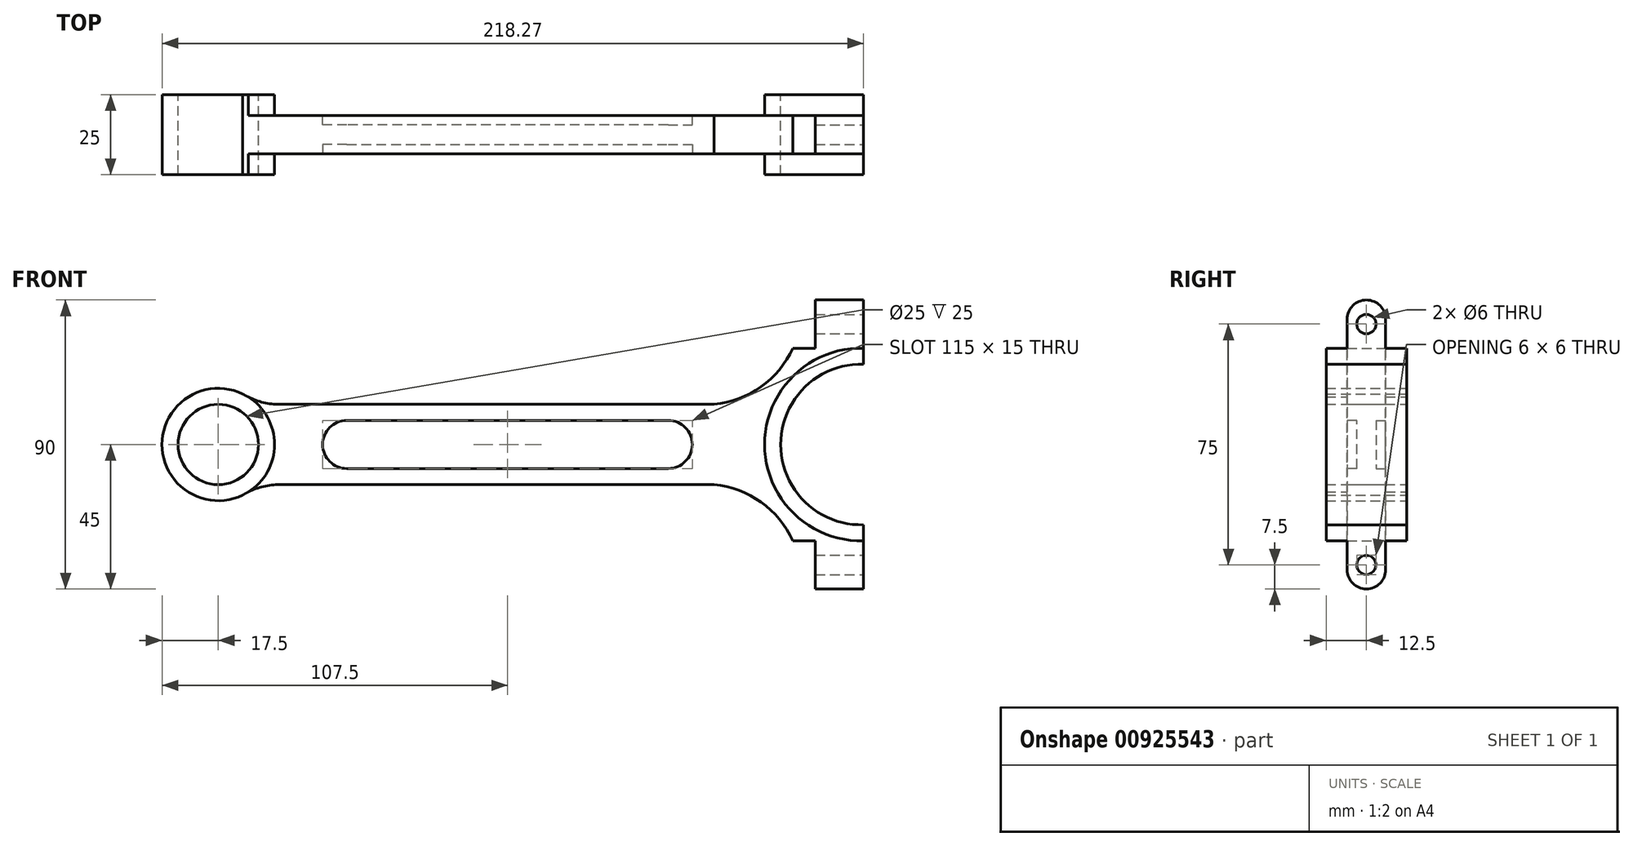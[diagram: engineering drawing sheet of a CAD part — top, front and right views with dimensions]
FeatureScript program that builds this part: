
annotation { "Feature Type Name" : "Feature", "Feature Type Description" : "" }
export const myFeature = defineFeature(function(context is Context, id is Id, definition is map)
    precondition{}
    {
        {
            var Q0;
            Q0=qCreatedBy(makeId("Front.planeOp"),FACE);
            var sketch = newSketch(context, id + "F0", { "sketchPlane" : qUnion([Q0])});
            skLineSegment(sketch, "E0", {"start": v(-127.43, 0) * mm, "end": v(160.56, 0) * mm, "construction": true});
            skCircle(sketch, "E1", {"center": v(-89.8, 0) * mm, "radius": 12.5 * mm});
            skCircle(sketch, "E2", {"center": v(-89.8, 0) * mm, "radius": 17.5 * mm});
            skArc(sketch, "E3", {"start": v(110.97, 24.99) * mm, "mid": v(85.2, 0) * mm, "end": v(110.97, -24.99) * mm});
            skLineSegment(sketch, "E4", {"start": v(110.97, -45) * mm, "end": v(95.97, -45) * mm});
            skLineSegment(sketch, "E5", {"start": v(95.97, -45) * mm, "end": v(95.97, -30) * mm});
            skLineSegment(sketch, "E6", {"start": v(110.97, 45) * mm, "end": v(95.97, 45) * mm});
            skLineSegment(sketch, "E7", {"start": v(95.97, 45) * mm, "end": v(95.97, 30) * mm});
            skLineSegment(sketch, "E8", {"start": v(95.97, 30) * mm, "end": v(88.97, 30) * mm});
            skLineSegment(sketch, "E9", {"start": v(95.97, -30) * mm, "end": v(88.97, -30) * mm});
            skLineSegment(sketch, "E10", {"start": v(110.97, 45) * mm, "end": v(110.97, 24.99) * mm});
            skLineSegment(sketch, "E11", {"start": v(110.97, -24.99) * mm, "end": v(110.97, -45) * mm});
            skArc(sketch, "E12", {"start": v(64.45, 12.5) * mm, "mid": v(79.06, 17.95) * mm, "end": v(88.97, 30) * mm});
            skArc(sketch, "E13", {"start": v(88.97, -30) * mm, "mid": v(79.06, -17.95) * mm, "end": v(64.45, -12.5) * mm});
            skLineSegment(sketch, "E14", {"start": v(64.45, 12.5) * mm, "end": v(-70.67, 12.5) * mm});
            skLineSegment(sketch, "E15", {"start": v(-70.67, -12.5) * mm, "end": v(64.45, -12.5) * mm});
            skArc(sketch, "E16", {"start": v(-82.18, 15.75) * mm, "mid": v(-76.65, 13.33) * mm, "end": v(-70.67, 12.5) * mm});
            skArc(sketch, "E17", {"start": v(-70.67, -12.5) * mm, "mid": v(-76.65, -13.33) * mm, "end": v(-82.18, -15.75) * mm});
            skArc(sketch, "E18", {"start": v(110.97, 30) * mm, "mid": v(80.2, 0) * mm, "end": v(110.97, -30) * mm});
            skSolve(sketch);
        }
        {
            var Q0;
            {var subQ0=sQuery(id+"F0.wireOp",EDGE,"E3");Q0=makeQuery(id+"F0.imprint","IMPRINT",FACE,{"disambiguationData":[TD([[makeQuery(id+"F0.imprint","IMPRINT",EDGE,{"derivedFrom":subQ0}),-1.0]])]});}
            var Q1;
            Q1=makeQuery(id+"F0.imprint","IMPRINT",FACE,{"disambiguationData":[TD([[makeQuery(id+"F0.imprint","IMPRINT",EDGE,{"derivedFrom":sQuery(id+"F0.wireOp",EDGE,"E1")}),-1.0]])]});
            extrude(context, id + "F1", {"entities" : qUnion([Q0, Q1]), "depth" : 25 * mm, "offsetDistance" : 25 * mm, "symmetric" : true});
        }
        {
            var Q0;
            {var subQ4=sQuery(id+"F0.wireOp",EDGE,"E4");Q0=makeQuery(id+"F0.imprint","IMPRINT",FACE,{"disambiguationData":[TD([[makeQuery(id+"F0.imprint","IMPRINT",EDGE,{"derivedFrom":subQ4}),-1.0]])]});}
            extrude(context, id + "F2", {"entities" : qUnion([Q0]), "operationType" : NewBodyOperationType.ADD, "depth" : 12 * mm, "offsetDistance" : 25 * mm, "symmetric" : true});
        }
        {
            var Q0;
            Q0=makeQuery(id+"F2.opExtrude","CAP_EDGE",EDGE,{"disambiguationData":[OSD([sQuery(id+"F0.wireOp",EDGE,"E6")])],"isStart":false});
            var Q1;
            Q1=makeQuery(id+"F2.opExtrude","CAP_EDGE",EDGE,{"disambiguationData":[OSD([sQuery(id+"F0.wireOp",EDGE,"E6")])],"isStart":true});
            fillet(context, id + "F3", {"entities" : qUnion([Q0, Q1]), "radius" : 6 * mm, "tangentPropagation" : true, "allowEdgeOverflow" : false});
        }
        {
            var Q0;
            Q0=makeQuery(id+"F2.opExtrude","CAP_EDGE",EDGE,{"disambiguationData":[OSD([sQuery(id+"F0.wireOp",EDGE,"E4")])],"isStart":false});
            var Q1;
            Q1=makeQuery(id+"F2.opExtrude","CAP_EDGE",EDGE,{"disambiguationData":[OSD([sQuery(id+"F0.wireOp",EDGE,"E4")])],"isStart":true});
            fillet(context, id + "F4", {"entities" : qUnion([Q0, Q1]), "radius" : 6 * mm, "tangentPropagation" : true, "allowEdgeOverflow" : false});
        }
        {
            var Q0;
            Q0=makeQuery(id+"F2.opExtrude","CAP_FACE",FACE,{"disambiguationData":[OSD([sQuery(id+"F0.wireOp",EDGE,"E2"),sQuery(id+"F0.wireOp",EDGE,"E4"),sQuery(id+"F0.wireOp",EDGE,"E5"),sQuery(id+"F0.wireOp",EDGE,"E6"),sQuery(id+"F0.wireOp",EDGE,"E7"),sQuery(id+"F0.wireOp",EDGE,"E8"),sQuery(id+"F0.wireOp",EDGE,"E9"),sQuery(id+"F0.wireOp",EDGE,"E10"),sQuery(id+"F0.wireOp",EDGE,"E11"),sQuery(id+"F0.wireOp",EDGE,"E12"),sQuery(id+"F0.wireOp",EDGE,"E13"),sQuery(id+"F0.wireOp",EDGE,"E14"),sQuery(id+"F0.wireOp",EDGE,"E15"),sQuery(id+"F0.wireOp",EDGE,"E16"),sQuery(id+"F0.wireOp",EDGE,"E17"),sQuery(id+"F0.wireOp",EDGE,"E18")])],"isStart":false});
            var sketch = newSketch(context, id + "F5", { "sketchPlane" : qUnion([Q0])});
            skLineSegment(sketch, "E19", {"start": v(-170.41, 0) * mm, "end": v(205.82, 0) * mm, "construction": true});
            skLineSegment(sketch, "E20", {"start": v(-49.8, 33.23) * mm, "end": v(-49.8, -32.69) * mm, "construction": true});
            skLineSegment(sketch, "E21", {"start": v(50.2, 34.53) * mm, "end": v(50.2, -44.84) * mm, "construction": true});
            skLineSegment(sketch, "E22", {"start": v(-49.8, 7.5) * mm, "end": v(50.2, 7.5) * mm});
            skLineSegment(sketch, "E23", {"start": v(-49.8, -7.5) * mm, "end": v(50.2, -7.5) * mm});
            skArc(sketch, "E24", {"start": v(50.2, 7.5) * mm, "mid": v(57.7, 0) * mm, "end": v(50.2, -7.5) * mm});
            skArc(sketch, "E25", {"start": v(-49.8, 7.5) * mm, "mid": v(-57.3, 0) * mm, "end": v(-49.8, -7.5) * mm});
            skPoint(sketch, "E26", {"position": v(-89.8, 0) * mm});
            skSolve(sketch);
        }
        {
            var Q0;
            Q0=makeQuery(id+"F5.imprint","IMPRINT",FACE,{"disambiguationData":[TD([[makeQuery(id+"F5.imprint","IMPRINT",EDGE,{"derivedFrom":sQuery(id+"F5.wireOp",EDGE,"E22")}),-1.0]])]});
            extrude(context, id + "F6", {"entities" : qUnion([Q0]), "operationType" : NewBodyOperationType.REMOVE, "oppositeDirection" : true, "depth" : 3 * mm, "offsetDistance" : 25 * mm});
        }
        {
            var Q0;
            Q0=makeQuery(id+"F2.opExtrude","CAP_FACE",FACE,{"disambiguationData":[OSD([sQuery(id+"F0.wireOp",EDGE,"E2"),sQuery(id+"F0.wireOp",EDGE,"E4"),sQuery(id+"F0.wireOp",EDGE,"E5"),sQuery(id+"F0.wireOp",EDGE,"E6"),sQuery(id+"F0.wireOp",EDGE,"E7"),sQuery(id+"F0.wireOp",EDGE,"E8"),sQuery(id+"F0.wireOp",EDGE,"E9"),sQuery(id+"F0.wireOp",EDGE,"E10"),sQuery(id+"F0.wireOp",EDGE,"E11"),sQuery(id+"F0.wireOp",EDGE,"E12"),sQuery(id+"F0.wireOp",EDGE,"E13"),sQuery(id+"F0.wireOp",EDGE,"E14"),sQuery(id+"F0.wireOp",EDGE,"E15"),sQuery(id+"F0.wireOp",EDGE,"E16"),sQuery(id+"F0.wireOp",EDGE,"E17"),sQuery(id+"F0.wireOp",EDGE,"E18")])],"isStart":true});
            var sketch = newSketch(context, id + "F7", { "sketchPlane" : qUnion([Q0])});
            skLineSegment(sketch, "E27", {"start": v(89.8, 0) * mm, "end": v(-155.32, 0) * mm, "construction": true});
            skLineSegment(sketch, "E28", {"start": v(-50.2, 21.6) * mm, "end": v(-50.2, -36.6) * mm, "construction": true});
            skLineSegment(sketch, "E29", {"start": v(49.8, 30.22) * mm, "end": v(49.8, -38.35) * mm, "construction": true});
            skLineSegment(sketch, "E30", {"start": v(-50.2, 7.5) * mm, "end": v(49.8, 7.5) * mm});
            skLineSegment(sketch, "E31", {"start": v(-50.2, -7.5) * mm, "end": v(49.8, -7.5) * mm});
            skArc(sketch, "E32", {"start": v(-50.2, 7.5) * mm, "mid": v(-57.7, 0) * mm, "end": v(-50.2, -7.5) * mm});
            skArc(sketch, "E33", {"start": v(49.8, 7.5) * mm, "mid": v(57.3, 0) * mm, "end": v(49.8, -7.5) * mm});
            skSolve(sketch);
        }
        {
            var Q0;
            Q0=makeQuery(id+"F7.imprint","IMPRINT",FACE,{"disambiguationData":[TD([[makeQuery(id+"F7.imprint","IMPRINT",EDGE,{"derivedFrom":sQuery(id+"F7.wireOp",EDGE,"E30")}),-1.0]])]});
            extrude(context, id + "F8", {"entities" : qUnion([Q0]), "operationType" : NewBodyOperationType.REMOVE, "oppositeDirection" : true, "depth" : 3 * mm, "offsetDistance" : 25 * mm});
        }
        {
            var Q0;
            {var subQ0=sQuery(id+"F0.wireOp",EDGE,"E10");Q0=makeQuery(id+"F2.boolean.opBoolean","MERGE",FACE,{"derivedFrom":[makeQuery(id+"F1.opExtrude","SWEPT_FACE",FACE,{"disambiguationData":[OSD([subQ0])]}),makeQuery(id+"F2.opExtrude","SWEPT_FACE",FACE,{"disambiguationData":[OSD([subQ0])]})]});}
            var sketch = newSketch(context, id + "F9", { "sketchPlane" : qUnion([Q0])});
            skLineSegment(sketch, "E34", {"start": v(0, 45) * mm, "end": v(0, -51.47) * mm, "construction": true});
            skLineSegment(sketch, "E35", {"start": v(-10.97, 37.5) * mm, "end": v(18.73, 37.5) * mm, "construction": true});
            skLineSegment(sketch, "E36", {"start": v(-11.67, -37.5) * mm, "end": v(22.44, -37.5) * mm, "construction": true});
            skPoint(sketch, "E37.0", {"position": v(0, -45) * mm});
            skPoint(sketch, "E38", {"position": v(0, 37.5) * mm});
            skPoint(sketch, "E39", {"position": v(0, -37.5) * mm});
            skCircle(sketch, "E40", {"center": v(0, 37.5) * mm, "radius": 3 * mm});
            skCircle(sketch, "E41", {"center": v(0, -37.5) * mm, "radius": 3 * mm});
            skSolve(sketch);
        }
        {
            var Q0;
            Q0=makeQuery(id+"F9.imprint","IMPRINT",FACE,{"disambiguationData":[TD([[makeQuery(id+"F9.imprint","IMPRINT",EDGE,{"derivedFrom":sQuery(id+"F9.wireOp",EDGE,"E40")}),1.0]])]});
            var Q1;
            Q1=makeQuery(id+"F9.imprint","IMPRINT",FACE,{"disambiguationData":[TD([[makeQuery(id+"F9.imprint","IMPRINT",EDGE,{"derivedFrom":sQuery(id+"F9.wireOp",EDGE,"E41")}),1.0]])]});
            extrude(context, id + "F10", {"entities" : qUnion([Q0, Q1]), "operationType" : NewBodyOperationType.REMOVE, "endBound" : BoundingType.THROUGH_ALL, "oppositeDirection" : true, "depth" : 25 * mm, "offsetDistance" : 25 * mm});
        }
    });
